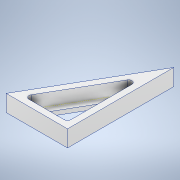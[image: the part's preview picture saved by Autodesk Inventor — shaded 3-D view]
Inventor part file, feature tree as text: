
AUTODESK INVENTOR PART (.ipt)
format: ipt  version: 2022 (Build 260153000, 153)  size: 138,240 bytes
history: native  units: mm
features: sketch x4, extrude x3, projected_geometry x2, fillet x1
ambient origin geometry x8: Origin, YZ Plane, XZ Plane, XY Plane, X Axis, Y Axis, Z Axis, Center Point
bodies: Solid1 (feature_tree)
feature tree (10):
  extrude  "Extrusion1"  Depth=147.8mm
  extrude  "Extrusion2"  Depth=15.0mm
  sketch  "Sketch3"  dims[d5=30.0mm d6=0.0mm d7=30.0deg d9=15.0mm]
  extrude  "Extrusion3"  TaperAngle=30.0deg  [1 undecoded]
  fillet  "Fillet2"  Radius=15.0mm
  sketch  "Sketch1"  dims[d0=256.0mm d1=147.8mm]
  sketch  "Sketch2"  dims[d2=40.0mm d3=0.0mm d4=15.0mm]
  projected_geometry  "Projected Loop1"
  sketch  "Sketch4"  dims[d10=30.0mm d11=0.0mm d12=8.0mm]
  projected_geometry  "Projected Loop2"
note: 1 required parameter value undecoded (feature->parameter linkage not recoverable at this tier; creation-order binding heuristic only, values carry confidence <= 0.55)
